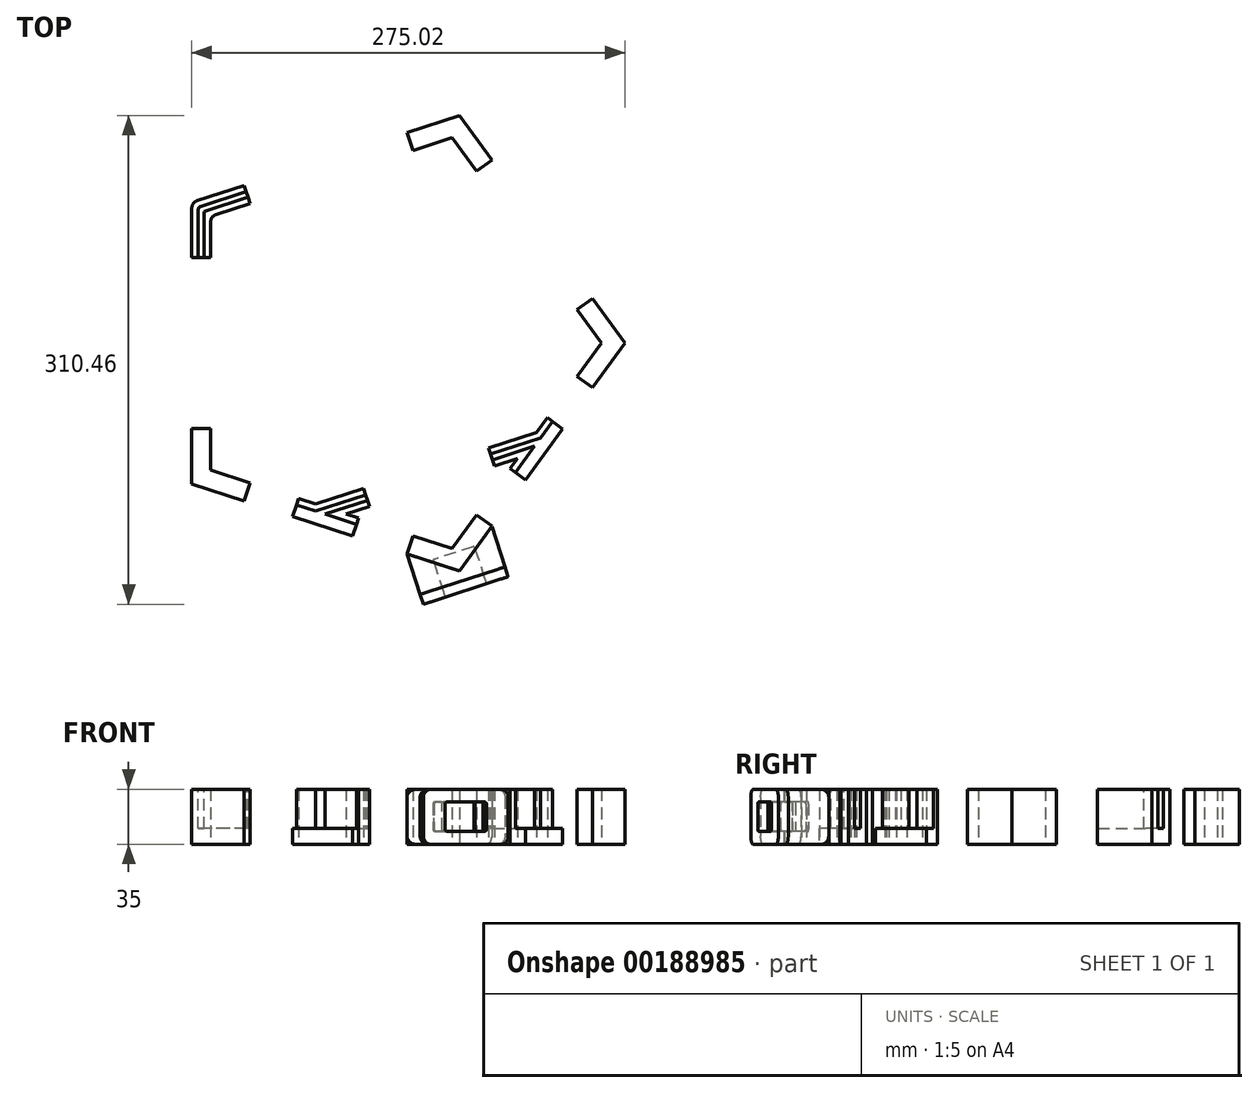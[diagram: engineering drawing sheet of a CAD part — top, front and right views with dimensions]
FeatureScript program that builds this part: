
annotation { "Feature Type Name" : "Feature", "Feature Type Description" : "" }
export const myFeature = defineFeature(function(context is Context, id is Id, definition is map)
    precondition{}
    {
        {
            var Q0;
            Q0=qCreatedBy(makeId("Top.planeOp"),FACE);
            var sketch = newSketch(context, id + "F0", { "sketchPlane" : qUnion([Q0])});
            skCircle(sketch, "E0.cCircle", {"center": v(0, 0) * mm, "radius": 117 * mm, "construction": true});
            skLineSegment(sketch, "E0.0", {"start": v(-117, 85) * mm, "end": v(44.69, 137.53) * mm, "construction": true});
            skLineSegment(sketch, "E0.1", {"start": v(44.69, 137.53) * mm, "end": v(144.61, 0) * mm, "construction": true});
            skLineSegment(sketch, "E0.2", {"start": v(144.61, 0) * mm, "end": v(44.69, -137.53) * mm, "construction": true});
            skLineSegment(sketch, "E0.3", {"start": v(44.69, -137.53) * mm, "end": v(-117, -85) * mm, "construction": true});
            skLineSegment(sketch, "E0.4", {"start": v(-117, -85) * mm, "end": v(-117, 85) * mm, "construction": true});
            skPoint(sketch, "E0.0.midPoint", {"position": v(-36.15, 111.27) * mm});
            skLineSegment(sketch, "E1", {"start": v(-123, 89.36) * mm, "end": v(-89.7, 100.17) * mm});
            skLineSegment(sketch, "E2", {"start": v(-123, 54.36) * mm, "end": v(-123, 89.36) * mm});
            skLineSegment(sketch, "E3.MirrorCS", {"start": v(-111, 54.36) * mm, "end": v(-111, 80.64) * mm});
            skLineSegment(sketch, "E4.MirrorCS", {"start": v(-111, 80.64) * mm, "end": v(-86, 88.76) * mm});
            skPoint(sketch, "E5.orphan", {"position": v(-127.63, 87.85) * mm});
            skPoint(sketch, "E6.orphan", {"position": v(-123, 104.04) * mm});
            skPoint(sketch, "E7.orphan", {"position": v(-111, 104.04) * mm});
            skPoint(sketch, "E8.orphan", {"position": v(-123.92, 76.44) * mm});
            skLineSegment(sketch, "E9", {"start": v(-123, 54.36) * mm, "end": v(-111, 54.36) * mm});
            skLineSegment(sketch, "E10", {"start": v(-86, 88.76) * mm, "end": v(-89.7, 100.17) * mm});
            skPoint(sketch, "E11.MirrorP", {"position": v(-127.63, -87.85) * mm});
            skPoint(sketch, "E12.MirrorP", {"position": v(-123, -104.04) * mm});
            skPoint(sketch, "E13.MirrorP", {"position": v(-111, -104.04) * mm});
            skPoint(sketch, "E14.MirrorP", {"position": v(-123.92, -76.44) * mm});
            skLineSegment(sketch, "E15.MirrorCS", {"start": v(-86, -88.76) * mm, "end": v(-89.7, -100.17) * mm});
            skLineSegment(sketch, "E16.MirrorCS", {"start": v(-123, -54.36) * mm, "end": v(-111, -54.36) * mm});
            skLineSegment(sketch, "E17.MirrorCS", {"start": v(-111, -80.64) * mm, "end": v(-86, -88.76) * mm});
            skLineSegment(sketch, "E18.MirrorCS", {"start": v(-111, -54.36) * mm, "end": v(-111, -80.64) * mm});
            skLineSegment(sketch, "E19.MirrorCS", {"start": v(-123, -54.36) * mm, "end": v(-123, -89.36) * mm});
            skLineSegment(sketch, "E20.MirrorCS", {"start": v(-123, -89.36) * mm, "end": v(-89.7, -100.17) * mm});
            skLineSegment(sketch, "E21.MirrorCS", {"start": v(-117, 85) * mm, "end": v(-117, -85) * mm, "construction": true});
            skLineSegment(sketch, "E22.MirrorCS", {"start": v(-117, -85) * mm, "end": v(44.69, -137.53) * mm, "construction": true});
            skLineSegment(sketch, "E23", {"start": v(-36.15, -111.27) * mm, "end": v(-46.52, -143.17) * mm, "construction": true});
            skLineSegment(sketch, "E24.MirrorCS", {"start": v(44.69, -137.53) * mm, "end": v(144.61, 0) * mm, "construction": true});
            skPoint(sketch, "E25.MirrorP", {"position": v(51.62, -146.1) * mm});
            skLineSegment(sketch, "E26.MirrorCS", {"start": v(67.55, -116.27) * mm, "end": v(46.98, -144.59) * mm});
            skPoint(sketch, "E27.MirrorP", {"position": v(160.66, 11.88) * mm});
            skLineSegment(sketch, "E28.MirrorCS", {"start": v(17.4, -122.36) * mm, "end": v(13.7, -133.77) * mm});
            skLineSegment(sketch, "E29.MirrorCS", {"start": v(121.75, 21.26) * mm, "end": v(131.45, 28.32) * mm});
            skLineSegment(sketch, "E30.MirrorCS", {"start": v(131.45, -28.32) * mm, "end": v(121.75, -21.26) * mm});
            skLineSegment(sketch, "E31.MirrorCS", {"start": v(137.2, 0) * mm, "end": v(121.75, 21.26) * mm});
            skLineSegment(sketch, "E32.MirrorCS", {"start": v(121.75, -21.26) * mm, "end": v(137.2, 0) * mm});
            skLineSegment(sketch, "E33.MirrorCS", {"start": v(131.45, -28.32) * mm, "end": v(152.03, 0) * mm});
            skLineSegment(sketch, "E34.MirrorCS", {"start": v(152.03, 0) * mm, "end": v(131.45, 28.32) * mm});
            skPoint(sketch, "E35.MirrorP", {"position": v(28.64, -149.41) * mm});
            skPoint(sketch, "E36.MirrorP", {"position": v(55.33, -134.68) * mm});
            skPoint(sketch, "E37.MirrorP", {"position": v(150.95, 18.93) * mm});
            skPoint(sketch, "E38.MirrorP", {"position": v(154.9, -3.95) * mm});
            skLineSegment(sketch, "E39.MirrorCS", {"start": v(67.55, -116.27) * mm, "end": v(57.84, -109.22) * mm});
            skLineSegment(sketch, "E40.MirrorCS", {"start": v(46.98, -144.59) * mm, "end": v(13.7, -133.77) * mm});
            skLineSegment(sketch, "E41.MirrorCS", {"start": v(42.4, -130.48) * mm, "end": v(17.4, -122.36) * mm});
            skLineSegment(sketch, "E42.MirrorCS", {"start": v(57.84, -109.22) * mm, "end": v(42.4, -130.48) * mm});
            skPoint(sketch, "E43.MirrorP", {"position": v(38.35, -156.47) * mm});
            skPoint(sketch, "E44.MirrorP", {"position": v(145.19, -11) * mm});
            skLineSegment(sketch, "E45", {"start": v(94.65, 68.77) * mm, "end": v(113.34, 82.34) * mm, "construction": true});
            skLineSegment(sketch, "E46.MirrorCS", {"start": v(44.69, 137.53) * mm, "end": v(-117, 85) * mm, "construction": true});
            skLineSegment(sketch, "E47.MirrorCS", {"start": v(46.98, 144.59) * mm, "end": v(67.55, 116.27) * mm});
            skPoint(sketch, "E48.MirrorP", {"position": v(60.94, 149.12) * mm});
            skPoint(sketch, "E49.MirrorP", {"position": v(44.11, 148.53) * mm});
            skPoint(sketch, "E50.MirrorP", {"position": v(34.4, 141.48) * mm});
            skLineSegment(sketch, "E51.MirrorCS", {"start": v(13.7, 133.77) * mm, "end": v(46.98, 144.59) * mm});
            skLineSegment(sketch, "E52.MirrorCS", {"start": v(42.4, 130.48) * mm, "end": v(57.84, 109.22) * mm});
            skPoint(sketch, "E53.MirrorP", {"position": v(64.65, 137.71) * mm});
            skLineSegment(sketch, "E54.MirrorCS", {"start": v(144.61, 0) * mm, "end": v(44.69, 137.53) * mm, "construction": true});
            skLineSegment(sketch, "E55.MirrorCS", {"start": v(57.84, 109.22) * mm, "end": v(67.55, 116.27) * mm});
            skLineSegment(sketch, "E56.MirrorCS", {"start": v(17.4, 122.36) * mm, "end": v(42.4, 130.48) * mm});
            skLineSegment(sketch, "E57.MirrorCS", {"start": v(13.7, 133.77) * mm, "end": v(17.4, 122.36) * mm});
            skLineSegment(sketch, "E58", {"start": v(-81.04, -120.55) * mm, "end": v(144.28, -47.34) * mm, "construction": true});
            skLineSegment(sketch, "E59", {"start": v(44.69, -137.53) * mm, "end": v(54.4, -134.38) * mm});
            skLineSegment(sketch, "E60", {"start": v(-20.95, -122.51) * mm, "end": v(-59, -110.15) * mm});
            skLineSegment(sketch, "E61.MirrorCS", {"start": v(-17.24, -111.1) * mm, "end": v(-24.89, -108.62) * mm});
            skLineSegment(sketch, "E62", {"start": v(-44.3, -102.3) * mm, "end": v(-13.87, -92.42) * mm});
            skLineSegment(sketch, "E63.MirrorCS", {"start": v(-34.6, -111.77) * mm, "end": v(-34.58, -111.77) * mm});
            skLineSegment(sketch, "E64", {"start": v(-55.29, -98.74) * mm, "end": v(-59, -110.15) * mm});
            skLineSegment(sketch, "E65", {"start": v(-17.24, -111.1) * mm, "end": v(-20.95, -122.51) * mm});
            skPoint(sketch, "E66.orphan", {"position": v(-40.6, -113.72) * mm});
            skLineSegment(sketch, "E67.trimOffspring", {"start": v(-24.89, -108.62) * mm, "end": v(-10.16, -103.83) * mm});
            skLineSegment(sketch, "E68.trimOffspring", {"start": v(-44.3, -102.3) * mm, "end": v(-55.29, -98.74) * mm});
            skLineSegment(sketch, "E69", {"start": v(-13.87, -92.42) * mm, "end": v(-10.16, -103.83) * mm});
            skLineSegment(sketch, "E70", {"start": v(-36.15, 111.27) * mm, "end": v(42.4, -130.48) * mm, "construction": true});
            skLineSegment(sketch, "E71.MirrorCS", {"start": v(93.69, -70.1) * mm, "end": v(93.67, -70.1) * mm});
            skLineSegment(sketch, "E72.MirrorCS", {"start": v(102.77, -47.39) * mm, "end": v(112.47, -54.44) * mm});
            skLineSegment(sketch, "E73.MirrorCS", {"start": v(95.98, -56.73) * mm, "end": v(102.77, -47.39) * mm});
            skLineSegment(sketch, "E74.MirrorCS", {"start": v(79.25, -79.75) * mm, "end": v(88.96, -86.8) * mm});
            skLineSegment(sketch, "E75.MirrorCS", {"start": v(95.98, -56.73) * mm, "end": v(65.55, -66.62) * mm});
            skPoint(sketch, "E76.MirrorP", {"position": v(99.69, -68.14) * mm});
            skLineSegment(sketch, "E77.MirrorCS", {"start": v(83.98, -73.24) * mm, "end": v(69.25, -78.03) * mm});
            skLineSegment(sketch, "E78.MirrorCS", {"start": v(88.96, -86.8) * mm, "end": v(112.47, -54.44) * mm});
            skLineSegment(sketch, "E79.MirrorCS", {"start": v(65.55, -66.62) * mm, "end": v(69.25, -78.03) * mm});
            skLineSegment(sketch, "E80.MirrorCS", {"start": v(79.25, -79.75) * mm, "end": v(83.98, -73.24) * mm});
            skLineSegment(sketch, "E81", {"start": v(22.07, -159.6) * mm, "end": v(75.94, -142.1) * mm});
            skLineSegment(sketch, "E82", {"start": v(67.59, -116.39) * mm, "end": v(75.94, -142.1) * mm});
            skLineSegment(sketch, "E83.MirrorCS", {"start": v(13.73, -133.89) * mm, "end": v(22.08, -159.6) * mm});
            skLineSegment(sketch, "E84", {"start": v(13.73, -133.89) * mm, "end": v(47.02, -144.7) * mm});
            skLineSegment(sketch, "E85", {"start": v(67.59, -116.39) * mm, "end": v(47.02, -144.7) * mm});
            skPoint(sketch, "E86.orphan", {"position": v(67.68, -116.27) * mm});
            skPoint(sketch, "E87.orphan", {"position": v(13.7, -133.77) * mm});
            skSolve(sketch);
        }
        {
            var Q0;
            Q0=qSketchRegion(id+"F0",true);
            extrude(context, id + "F1", {"entities" : qUnion([Q0]), "depth" : 35 * mm});
        }
        {
            var Q0;
            Q0=makeQuery(id+"F1.opExtrude","CAP_FACE",FACE,{"disambiguationData":[OSD([sQuery(id+"F0.wireOp",EDGE,"E1"),sQuery(id+"F0.wireOp",EDGE,"E2"),sQuery(id+"F0.wireOp",EDGE,"E3.MirrorCS"),sQuery(id+"F0.wireOp",EDGE,"E4.MirrorCS"),sQuery(id+"F0.wireOp",EDGE,"E9"),sQuery(id+"F0.wireOp",EDGE,"E10")])],"isStart":false});
            var sketch = newSketch(context, id + "F2", { "sketchPlane" : qUnion([Q0])});
            skLineSegment(sketch, "E88", {"start": v(-117, 54.36) * mm, "end": v(-117, 85) * mm});
            skLineSegment(sketch, "E89", {"start": v(-87.85, 94.47) * mm, "end": v(-117, 85) * mm});
            skPoint(sketch, "E90.orphan", {"position": v(-117, 84.36) * mm});
            skPoint(sketch, "E91.orphan", {"position": v(-118.96, 84.36) * mm});
            skArc(sketch, "E92.0.startCap", {"start": v(-115.12, 54.36) * mm, "mid": v(-117, 52.48) * mm, "end": v(-118.87, 54.36) * mm});
            skArc(sketch, "E92.0.endCap", {"start": v(-118.87, 85) * mm, "mid": v(-117, 86.87) * mm, "end": v(-115.12, 85) * mm});
            skLineSegment(sketch, "E92.0.left", {"start": v(-118.87, 54.36) * mm, "end": v(-118.87, 85) * mm});
            skLineSegment(sketch, "E92.0.right", {"start": v(-115.12, 54.36) * mm, "end": v(-115.12, 85) * mm});
            skArc(sketch, "E92.1.startCap", {"start": v(-88.43, 96.25) * mm, "mid": v(-86.07, 95.05) * mm, "end": v(-87.27, 92.69) * mm});
            skArc(sketch, "E92.1.endCap", {"start": v(-116.41, 83.22) * mm, "mid": v(-118.78, 84.42) * mm, "end": v(-117.57, 86.78) * mm});
            skLineSegment(sketch, "E92.1.left", {"start": v(-87.27, 92.69) * mm, "end": v(-116.41, 83.22) * mm});
            skLineSegment(sketch, "E92.1.right", {"start": v(-88.43, 96.25) * mm, "end": v(-117.57, 86.78) * mm});
            skLineSegment(sketch, "E93", {"start": v(-44.3, -108.62) * mm, "end": v(99.69, -61.83) * mm});
            skLineSegment(sketch, "E94", {"start": v(113.08, -43.4) * mm, "end": v(77.1, -92.92) * mm});
            skLineSegment(sketch, "E95", {"start": v(-66.96, -101.26) * mm, "end": v(-1.1, -122.66) * mm});
            skPoint(sketch, "E96.end.orphan", {"position": v(64.77, -144.06) * mm});
            skArc(sketch, "E97.0.startCap", {"start": v(-43.73, -110.4) * mm, "mid": v(-46.09, -109.2) * mm, "end": v(-44.88, -106.83) * mm});
            skArc(sketch, "E97.0.endCap", {"start": v(99.1, -60.05) * mm, "mid": v(101.47, -61.25) * mm, "end": v(100.27, -63.62) * mm});
            skLineSegment(sketch, "E97.0.left", {"start": v(-44.88, -106.83) * mm, "end": v(99.1, -60.05) * mm});
            skLineSegment(sketch, "E97.0.right", {"start": v(-43.73, -110.4) * mm, "end": v(100.27, -63.62) * mm});
            skArc(sketch, "E97.1.startCap", {"start": v(-67.54, -103.04) * mm, "mid": v(-68.74, -100.68) * mm, "end": v(-66.38, -99.47) * mm});
            skArc(sketch, "E97.1.endCap", {"start": v(-0.51, -120.87) * mm, "mid": v(0.7, -123.24) * mm, "end": v(-1.67, -124.44) * mm});
            skLineSegment(sketch, "E97.1.left", {"start": v(-66.38, -99.47) * mm, "end": v(-0.51, -120.87) * mm});
            skLineSegment(sketch, "E97.1.right", {"start": v(-67.54, -103.04) * mm, "end": v(-1.67, -124.44) * mm});
            skArc(sketch, "E97.2.startCap", {"start": v(111.56, -42.3) * mm, "mid": v(114.18, -41.88) * mm, "end": v(114.6, -44.5) * mm});
            skArc(sketch, "E97.2.endCap", {"start": v(78.61, -94.03) * mm, "mid": v(76, -94.44) * mm, "end": v(75.58, -91.82) * mm});
            skLineSegment(sketch, "E97.2.left", {"start": v(114.6, -44.5) * mm, "end": v(78.61, -94.03) * mm});
            skLineSegment(sketch, "E97.2.right", {"start": v(111.56, -42.3) * mm, "end": v(75.58, -91.82) * mm});
            skSolve(sketch);
        }
        {
            var Q0;
            {var subQ0=sQuery(id+"F2.wireOp",EDGE,"E97.1.endCap");Q0=makeQuery(id+"F2.imprint","IMPRINT",FACE,{"disambiguationData":[TD([[makeQuery(id+"F2.imprint","IMPRINT",EDGE,{"derivedFrom":subQ0}),-1.0]])]});}
            var Q1;
            {var subQ5=sQuery(id+"F2.wireOp",EDGE,"E97.1.startCap");Q1=makeQuery(id+"F2.imprint","IMPRINT",FACE,{"disambiguationData":[TD([[makeQuery(id+"F2.imprint","IMPRINT",EDGE,{"derivedFrom":subQ5}),-1.0]])]});}
            var Q2;
            {var subQ8=sQuery(id+"F2.wireOp",EDGE,"E97.2.startCap");Q2=makeQuery(id+"F2.imprint","IMPRINT",FACE,{"disambiguationData":[TD([[makeQuery(id+"F2.imprint","IMPRINT",EDGE,{"derivedFrom":subQ8}),-1.0]])]});}
            var Q3;
            {var subQ5=sQuery(id+"F2.wireOp",EDGE,"E97.2.endCap");Q3=makeQuery(id+"F2.imprint","IMPRINT",FACE,{"disambiguationData":[TD([[makeQuery(id+"F2.imprint","IMPRINT",EDGE,{"derivedFrom":subQ5}),-1.0]])]});}
            var Q4;
            {var subQ3=sQuery(id+"F2.wireOp",EDGE,"E89");var subQ7=sQuery(id+"F2.wireOp",EDGE,"E88");var subQ8=makeQuery(id+"F2.imprint","INTERSECT",VERTEX,{"derivedFrom":[subQ7,subQ3]});Q4=makeQuery(id+"F2.imprint","IMPRINT",FACE,{"disambiguationData":[TD([[makeQuery(id+"F2.imprint","IMPRINT",EDGE,{"disambiguationData":[TD([[subQ8,1.0]])],"derivedFrom":subQ7}),-1.0]])]});}
            var Q5;
            {var subQ0=sQuery(id+"F2.wireOp",EDGE,"E97.1.left");var subQ1=sQuery(id+"F2.wireOp",EDGE,"E93");var subQ2=makeQuery(id+"F2.imprint","INTERSECT",VERTEX,{"derivedFrom":[subQ1,subQ0]});Q5=makeQuery(id+"F2.imprint","IMPRINT",FACE,{"disambiguationData":[TD([[makeQuery(id+"F2.imprint","IMPRINT",EDGE,{"disambiguationData":[TD([[subQ2,-1.0]])],"derivedFrom":subQ1}),1.0]])]});}
            var Q6;
            {var subQ2=sQuery(id+"F2.wireOp",EDGE,"E88");var subQ6=sQuery(id+"F2.wireOp",EDGE,"E89");var subQ8=makeQuery(id+"F2.imprint","INTERSECT",VERTEX,{"derivedFrom":[subQ2,subQ6]});Q6=makeQuery(id+"F2.imprint","IMPRINT",FACE,{"disambiguationData":[TD([[makeQuery(id+"F2.imprint","IMPRINT",EDGE,{"disambiguationData":[TD([[subQ8,1.0]])],"derivedFrom":subQ2}),1.0]])]});}
            var Q7;
            {var subQ3=sQuery(id+"F2.wireOp",EDGE,"E95");var subQ7=sQuery(id+"F2.wireOp",EDGE,"E93");var subQ8=makeQuery(id+"F2.imprint","INTERSECT",VERTEX,{"derivedFrom":[subQ7,subQ3]});Q7=makeQuery(id+"F2.imprint","IMPRINT",FACE,{"disambiguationData":[TD([[makeQuery(id+"F2.imprint","IMPRINT",EDGE,{"disambiguationData":[TD([[subQ8,-1.0]])],"derivedFrom":subQ7}),1.0]])]});}
            var Q8;
            {var subQ0=sQuery(id+"F2.wireOp",EDGE,"E95");var subQ1=sQuery(id+"F2.wireOp",EDGE,"E93");var subQ2=makeQuery(id+"F2.imprint","INTERSECT",VERTEX,{"derivedFrom":[subQ1,subQ0]});Q8=makeQuery(id+"F2.imprint","IMPRINT",FACE,{"disambiguationData":[TD([[makeQuery(id+"F2.imprint","IMPRINT",EDGE,{"disambiguationData":[TD([[subQ2,-1.0]])],"derivedFrom":subQ1}),-1.0]])]});}
            var Q9;
            {var subQ5=sQuery(id+"F2.wireOp",EDGE,"E94");var subQ6=sQuery(id+"F2.wireOp",EDGE,"E93");var subQ7=makeQuery(id+"F2.imprint","INTERSECT",VERTEX,{"derivedFrom":[subQ6,subQ5]});Q9=makeQuery(id+"F2.imprint","IMPRINT",FACE,{"disambiguationData":[TD([[makeQuery(id+"F2.imprint","IMPRINT",EDGE,{"disambiguationData":[TD([[subQ7,1.0]])],"derivedFrom":subQ6}),1.0]])]});}
            var Q10;
            {var subQ0=sQuery(id+"F2.wireOp",EDGE,"E94");var subQ1=sQuery(id+"F2.wireOp",EDGE,"E93");var subQ2=makeQuery(id+"F2.imprint","INTERSECT",VERTEX,{"derivedFrom":[subQ1,subQ0]});Q10=makeQuery(id+"F2.imprint","IMPRINT",FACE,{"disambiguationData":[TD([[makeQuery(id+"F2.imprint","IMPRINT",EDGE,{"disambiguationData":[TD([[subQ2,1.0]])],"derivedFrom":subQ1}),-1.0]])]});}
            var Q11;
            {var subQ4=sQuery(id+"F2.wireOp",EDGE,"E94");var subQ5=makeQuery(id+"F2.imprint","INTERSECT",VERTEX,{"derivedFrom":[sQuery(id+"F2.wireOp",EDGE,"E93"),subQ4]});Q11=makeQuery(id+"F2.imprint","IMPRINT",FACE,{"disambiguationData":[TD([[makeQuery(id+"F2.imprint","IMPRINT",EDGE,{"disambiguationData":[TD([[subQ5,1.0]])],"derivedFrom":subQ4}),1.0]])]});}
            var Q12;
            {var subQ1=sQuery(id+"F2.wireOp",EDGE,"E95");var subQ4=makeQuery(id+"F2.imprint","INTERSECT",VERTEX,{"derivedFrom":[sQuery(id+"F2.wireOp",EDGE,"E93"),subQ1]});Q12=makeQuery(id+"F2.imprint","IMPRINT",FACE,{"disambiguationData":[TD([[makeQuery(id+"F2.imprint","IMPRINT",EDGE,{"disambiguationData":[TD([[subQ4,1.0]])],"derivedFrom":subQ1}),-1.0]])]});}
            var Q13;
            {var subQ5=sQuery(id+"F2.wireOp",EDGE,"E92.0.left");Q13=makeQuery(id+"F2.imprint","IMPRINT",FACE,{"disambiguationData":[TD([[makeQuery(id+"F2.imprint","IMPRINT",EDGE,{"derivedFrom":subQ5}),-1.0]])]});}
            var Q14;
            {var subQ5=sQuery(id+"F2.wireOp",EDGE,"E88");var subQ7=makeQuery(id+"F1.opExtrude","CAP_EDGE",EDGE,{"disambiguationData":[OSD([sQuery(id+"F0.wireOp",EDGE,"E9")])],"isStart":false});var subQ9=makeQuery(id+"F2.imprint","INTERSECT",VERTEX,{"derivedFrom":[subQ7,subQ5]});Q14=makeQuery(id+"F2.imprint","IMPRINT",FACE,{"disambiguationData":[TD([[makeQuery(id+"F2.imprint","IMPRINT",EDGE,{"disambiguationData":[TD([[subQ9,-1.0]])],"derivedFrom":subQ5}),-1.0]])]});}
            var Q15;
            {var subQ5=sQuery(id+"F2.wireOp",EDGE,"E92.1.right");Q15=makeQuery(id+"F2.imprint","IMPRINT",FACE,{"disambiguationData":[TD([[makeQuery(id+"F2.imprint","IMPRINT",EDGE,{"derivedFrom":subQ5}),1.0]])]});}
            var Q16;
            {var subQ1=makeQuery(id+"F1.opExtrude","CAP_EDGE",EDGE,{"disambiguationData":[OSD([sQuery(id+"F0.wireOp",EDGE,"E10")])],"isStart":false});var subQ7=sQuery(id+"F2.wireOp",EDGE,"E89");var subQ9=makeQuery(id+"F2.imprint","INTERSECT",VERTEX,{"derivedFrom":[subQ1,subQ7]});Q16=makeQuery(id+"F2.imprint","IMPRINT",FACE,{"disambiguationData":[TD([[makeQuery(id+"F2.imprint","IMPRINT",EDGE,{"disambiguationData":[TD([[subQ9,-1.0]])],"derivedFrom":subQ7}),1.0]])]});}
            var Q17;
            {var subQ0=sQuery(id+"F2.wireOp",EDGE,"E92.0.startCap");Q17=makeQuery(id+"F2.imprint","IMPRINT",FACE,{"disambiguationData":[TD([[makeQuery(id+"F2.imprint","IMPRINT",EDGE,{"derivedFrom":subQ0}),-1.0]])]});}
            var Q18;
            {var subQ0=sQuery(id+"F2.wireOp",EDGE,"E92.1.startCap");Q18=makeQuery(id+"F2.imprint","IMPRINT",FACE,{"disambiguationData":[TD([[makeQuery(id+"F2.imprint","IMPRINT",EDGE,{"derivedFrom":subQ0}),-1.0]])]});}
            extrude(context, id + "F3", {"entities" : qUnion([Q0, Q1, Q2, Q3, Q4, Q5, Q6, Q7, Q8, Q9, Q10, Q11, Q12, Q13, Q14, Q15, Q16, Q17, Q18]), "operationType" : NewBodyOperationType.REMOVE, "oppositeDirection" : true, "depth" : 25 * mm});
        }
        {
            var Q0;
            Q0=makeQuery(id+"F1.opExtrude","SWEPT_EDGE",EDGE,{"disambiguationData":[OSD([sQuery(id+"F0.wireOp",EDGE,"E3.MirrorCS"),sQuery(id+"F0.wireOp",EDGE,"E4.MirrorCS")])]});
            var Q1;
            Q1=makeQuery(id+"F1.opExtrude","SWEPT_EDGE",EDGE,{"disambiguationData":[OSD([sQuery(id+"F0.wireOp",EDGE,"E1"),sQuery(id+"F0.wireOp",EDGE,"E2")])]});
            fillet(context, id + "F4", {"entities" : qUnion([Q0, Q1]), "radius" : 5 * mm, "tangentPropagation" : true, "allowEdgeOverflow" : false});
        }
        {
            var Q0;
            Q0=makeQuery(id+"F1.opExtrude","CAP_FACE",FACE,{"disambiguationData":[OSD([sQuery(id+"F0.wireOp",EDGE,"E60"),sQuery(id+"F0.wireOp",EDGE,"E61.MirrorCS"),sQuery(id+"F0.wireOp",EDGE,"E62"),sQuery(id+"F0.wireOp",EDGE,"E64"),sQuery(id+"F0.wireOp",EDGE,"E65"),sQuery(id+"F0.wireOp",EDGE,"E67.trimOffspring"),sQuery(id+"F0.wireOp",EDGE,"E68.trimOffspring"),sQuery(id+"F0.wireOp",EDGE,"E69")])],"isStart":false});
            var sketch = newSketch(context, id + "F5", { "sketchPlane" : qUnion([Q0])});
            skLineSegment(sketch, "E98", {"start": v(-44.3, -108.62) * mm, "end": v(99.69, -61.83) * mm});
            skLineSegment(sketch, "E99", {"start": v(112.9, -43.64) * mm, "end": v(76.92, -93.16) * mm});
            skLineSegment(sketch, "E100", {"start": v(-67.46, -101.1) * mm, "end": v(-1.6, -122.5) * mm});
            skPoint(sketch, "E101.end.orphan", {"position": v(64.27, -143.9) * mm});
            skArc(sketch, "E102.0.startCap", {"start": v(-43.73, -110.4) * mm, "mid": v(-46.09, -109.2) * mm, "end": v(-44.88, -106.83) * mm});
            skArc(sketch, "E102.0.endCap", {"start": v(99.1, -60.05) * mm, "mid": v(101.47, -61.25) * mm, "end": v(100.27, -63.62) * mm});
            skLineSegment(sketch, "E102.0.left", {"start": v(-44.88, -106.83) * mm, "end": v(99.1, -60.05) * mm});
            skLineSegment(sketch, "E102.0.right", {"start": v(-43.73, -110.4) * mm, "end": v(100.27, -63.62) * mm});
            skArc(sketch, "E102.1.startCap", {"start": v(-68.04, -102.88) * mm, "mid": v(-69.25, -100.51) * mm, "end": v(-66.88, -99.3) * mm});
            skArc(sketch, "E102.1.endCap", {"start": v(-1.02, -120.71) * mm, "mid": v(0.19, -123.07) * mm, "end": v(-2.18, -124.28) * mm});
            skLineSegment(sketch, "E102.1.left", {"start": v(-66.88, -99.3) * mm, "end": v(-1.02, -120.71) * mm});
            skLineSegment(sketch, "E102.1.right", {"start": v(-68.04, -102.88) * mm, "end": v(-2.18, -124.28) * mm});
            skArc(sketch, "E102.2.startCap", {"start": v(111.4, -42.53) * mm, "mid": v(114, -42.12) * mm, "end": v(114.42, -44.74) * mm});
            skArc(sketch, "E102.2.endCap", {"start": v(78.44, -94.27) * mm, "mid": v(75.82, -94.68) * mm, "end": v(75.4, -92.06) * mm});
            skLineSegment(sketch, "E102.2.left", {"start": v(114.42, -44.74) * mm, "end": v(78.44, -94.27) * mm});
            skLineSegment(sketch, "E102.2.right", {"start": v(111.4, -42.53) * mm, "end": v(75.4, -92.06) * mm});
            skSolve(sketch);
        }
        {
            var Q0;
            {var subQ1=sQuery(id+"F5.wireOp",EDGE,"E102.1.startCap");Q0=makeQuery(id+"F5.imprint","IMPRINT",FACE,{"disambiguationData":[TD([[makeQuery(id+"F5.imprint","IMPRINT",EDGE,{"derivedFrom":subQ1}),-1.0]])]});}
            var Q1;
            {var subQ5=sQuery(id+"F5.wireOp",EDGE,"E102.0.startCap");var subQ7=sQuery(id+"F5.wireOp",EDGE,"E100");var subQ8=makeQuery(id+"F5.imprint","INTERSECT",VERTEX,{"derivedFrom":[subQ7,subQ5]});Q1=makeQuery(id+"F5.imprint","IMPRINT",FACE,{"disambiguationData":[TD([[makeQuery(id+"F5.imprint","IMPRINT",EDGE,{"disambiguationData":[TD([[subQ8,1.0]])],"derivedFrom":subQ7}),1.0]])]});}
            var Q2;
            {var subQ0=sQuery(id+"F5.wireOp",EDGE,"E102.0.startCap");var subQ1=sQuery(id+"F5.wireOp",EDGE,"E100");var subQ2=makeQuery(id+"F5.imprint","INTERSECT",VERTEX,{"derivedFrom":[subQ1,subQ0]});Q2=makeQuery(id+"F5.imprint","IMPRINT",FACE,{"disambiguationData":[TD([[makeQuery(id+"F5.imprint","IMPRINT",EDGE,{"disambiguationData":[TD([[subQ2,1.0]])],"derivedFrom":subQ1}),-1.0]])]});}
            var Q3;
            {var subQ1=sQuery(id+"F5.wireOp",EDGE,"E100");var subQ6=makeQuery(id+"F5.imprint","INTERSECT",VERTEX,{"derivedFrom":[sQuery(id+"F5.wireOp",EDGE,"E98"),subQ1]});Q3=makeQuery(id+"F5.imprint","IMPRINT",FACE,{"disambiguationData":[TD([[makeQuery(id+"F5.imprint","IMPRINT",EDGE,{"disambiguationData":[TD([[subQ6,1.0]])],"derivedFrom":subQ1}),-1.0]])]});}
            var Q4;
            {var subQ3=sQuery(id+"F5.wireOp",EDGE,"E100");var subQ5=sQuery(id+"F5.wireOp",EDGE,"E98");var subQ6=makeQuery(id+"F5.imprint","INTERSECT",VERTEX,{"derivedFrom":[subQ5,subQ3]});Q4=makeQuery(id+"F5.imprint","IMPRINT",FACE,{"disambiguationData":[TD([[makeQuery(id+"F5.imprint","IMPRINT",EDGE,{"disambiguationData":[TD([[subQ6,-1.0]])],"derivedFrom":subQ5}),1.0]])]});}
            var Q5;
            {var subQ0=sQuery(id+"F5.wireOp",EDGE,"E100");var subQ1=sQuery(id+"F5.wireOp",EDGE,"E98");var subQ2=makeQuery(id+"F5.imprint","INTERSECT",VERTEX,{"derivedFrom":[subQ1,subQ0]});Q5=makeQuery(id+"F5.imprint","IMPRINT",FACE,{"disambiguationData":[TD([[makeQuery(id+"F5.imprint","IMPRINT",EDGE,{"disambiguationData":[TD([[subQ2,-1.0]])],"derivedFrom":subQ1}),-1.0]])]});}
            var Q6;
            {var subQ0=sQuery(id+"F5.wireOp",EDGE,"E102.1.left");var subQ1=sQuery(id+"F5.wireOp",EDGE,"E98");var subQ2=makeQuery(id+"F5.imprint","INTERSECT",VERTEX,{"derivedFrom":[subQ1,subQ0]});Q6=makeQuery(id+"F5.imprint","IMPRINT",FACE,{"disambiguationData":[TD([[makeQuery(id+"F5.imprint","IMPRINT",EDGE,{"disambiguationData":[TD([[subQ2,-1.0]])],"derivedFrom":subQ1}),1.0]])]});}
            var Q7;
            {var subQ0=sQuery(id+"F5.wireOp",EDGE,"E102.1.left");var subQ1=sQuery(id+"F5.wireOp",EDGE,"E98");var subQ2=makeQuery(id+"F5.imprint","INTERSECT",VERTEX,{"derivedFrom":[subQ1,subQ0]});Q7=makeQuery(id+"F5.imprint","IMPRINT",FACE,{"disambiguationData":[TD([[makeQuery(id+"F5.imprint","IMPRINT",EDGE,{"disambiguationData":[TD([[subQ2,-1.0]])],"derivedFrom":subQ1}),-1.0]])]});}
            var Q8;
            {var subQ0=sQuery(id+"F5.wireOp",EDGE,"E102.0.right");var subQ1=sQuery(id+"F5.wireOp",EDGE,"E100");var subQ2=makeQuery(id+"F5.imprint","INTERSECT",VERTEX,{"derivedFrom":[subQ1,subQ0]});Q8=makeQuery(id+"F5.imprint","IMPRINT",FACE,{"disambiguationData":[TD([[makeQuery(id+"F5.imprint","IMPRINT",EDGE,{"disambiguationData":[TD([[subQ2,-1.0]])],"derivedFrom":subQ1}),1.0]])]});}
            var Q9;
            {var subQ5=sQuery(id+"F5.wireOp",EDGE,"E102.0.right");var subQ7=sQuery(id+"F5.wireOp",EDGE,"E100");var subQ8=makeQuery(id+"F5.imprint","INTERSECT",VERTEX,{"derivedFrom":[subQ7,subQ5]});Q9=makeQuery(id+"F5.imprint","IMPRINT",FACE,{"disambiguationData":[TD([[makeQuery(id+"F5.imprint","IMPRINT",EDGE,{"disambiguationData":[TD([[subQ8,-1.0]])],"derivedFrom":subQ7}),-1.0]])]});}
            var Q10;
            {var subQ1=sQuery(id+"F5.wireOp",EDGE,"E102.1.endCap");Q10=makeQuery(id+"F5.imprint","IMPRINT",FACE,{"disambiguationData":[TD([[makeQuery(id+"F5.imprint","IMPRINT",EDGE,{"derivedFrom":subQ1}),-1.0]])]});}
            var Q11;
            {var subQ0=sQuery(id+"F5.wireOp",EDGE,"E102.2.right");var subQ1=sQuery(id+"F5.wireOp",EDGE,"E98");var subQ2=makeQuery(id+"F5.imprint","INTERSECT",VERTEX,{"derivedFrom":[subQ1,subQ0]});Q11=makeQuery(id+"F5.imprint","IMPRINT",FACE,{"disambiguationData":[TD([[makeQuery(id+"F5.imprint","IMPRINT",EDGE,{"disambiguationData":[TD([[subQ2,1.0]])],"derivedFrom":subQ1}),-1.0]])]});}
            var Q12;
            {var subQ0=sQuery(id+"F5.wireOp",EDGE,"E102.2.right");var subQ1=sQuery(id+"F5.wireOp",EDGE,"E98");var subQ2=makeQuery(id+"F5.imprint","INTERSECT",VERTEX,{"derivedFrom":[subQ1,subQ0]});Q12=makeQuery(id+"F5.imprint","IMPRINT",FACE,{"disambiguationData":[TD([[makeQuery(id+"F5.imprint","IMPRINT",EDGE,{"disambiguationData":[TD([[subQ2,1.0]])],"derivedFrom":subQ1}),1.0]])]});}
            var Q13;
            {var subQ4=sQuery(id+"F5.wireOp",EDGE,"E99");var subQ6=makeQuery(id+"F5.imprint","INTERSECT",VERTEX,{"derivedFrom":[sQuery(id+"F5.wireOp",EDGE,"E98"),subQ4]});Q13=makeQuery(id+"F5.imprint","IMPRINT",FACE,{"disambiguationData":[TD([[makeQuery(id+"F5.imprint","IMPRINT",EDGE,{"disambiguationData":[TD([[subQ6,1.0]])],"derivedFrom":subQ4}),1.0]])]});}
            var Q14;
            {var subQ5=sQuery(id+"F5.wireOp",EDGE,"E99");var subQ6=sQuery(id+"F5.wireOp",EDGE,"E98");var subQ7=makeQuery(id+"F5.imprint","INTERSECT",VERTEX,{"derivedFrom":[subQ6,subQ5]});Q14=makeQuery(id+"F5.imprint","IMPRINT",FACE,{"disambiguationData":[TD([[makeQuery(id+"F5.imprint","IMPRINT",EDGE,{"disambiguationData":[TD([[subQ7,1.0]])],"derivedFrom":subQ6}),1.0]])]});}
            var Q15;
            {var subQ0=sQuery(id+"F5.wireOp",EDGE,"E99");var subQ1=sQuery(id+"F5.wireOp",EDGE,"E98");var subQ2=makeQuery(id+"F5.imprint","INTERSECT",VERTEX,{"derivedFrom":[subQ1,subQ0]});Q15=makeQuery(id+"F5.imprint","IMPRINT",FACE,{"disambiguationData":[TD([[makeQuery(id+"F5.imprint","IMPRINT",EDGE,{"disambiguationData":[TD([[subQ2,1.0]])],"derivedFrom":subQ1}),-1.0]])]});}
            var Q16;
            {var subQ0=sQuery(id+"F5.wireOp",EDGE,"E102.2.endCap");Q16=makeQuery(id+"F5.imprint","IMPRINT",FACE,{"disambiguationData":[TD([[makeQuery(id+"F5.imprint","IMPRINT",EDGE,{"derivedFrom":subQ0}),-1.0]])]});}
            var Q17;
            {var subQ0=sQuery(id+"F5.wireOp",EDGE,"E102.2.startCap");Q17=makeQuery(id+"F5.imprint","IMPRINT",FACE,{"disambiguationData":[TD([[makeQuery(id+"F5.imprint","IMPRINT",EDGE,{"derivedFrom":subQ0}),-1.0]])]});}
            extrude(context, id + "F6", {"entities" : qUnion([Q0, Q1, Q2, Q3, Q4, Q5, Q6, Q7, Q8, Q9, Q10, Q11, Q12, Q13, Q14, Q15, Q16, Q17]), "operationType" : NewBodyOperationType.REMOVE, "oppositeDirection" : true, "depth" : 25 * mm});
        }
        {
            var Q0;
            Q0=makeQuery(id+"F1.opExtrude","CAP_FACE",FACE,{"disambiguationData":[OSD([sQuery(id+"F0.wireOp",EDGE,"E72.MirrorCS"),sQuery(id+"F0.wireOp",EDGE,"E73.MirrorCS"),sQuery(id+"F0.wireOp",EDGE,"E74.MirrorCS"),sQuery(id+"F0.wireOp",EDGE,"E75.MirrorCS"),sQuery(id+"F0.wireOp",EDGE,"E77.MirrorCS"),sQuery(id+"F0.wireOp",EDGE,"E78.MirrorCS"),sQuery(id+"F0.wireOp",EDGE,"E79.MirrorCS"),sQuery(id+"F0.wireOp",EDGE,"E80.MirrorCS")])],"isStart":false});
            var sketch = newSketch(context, id + "F7", { "sketchPlane" : qUnion([Q0])});
            skLineSegment(sketch, "E103", {"start": v(-44.5, -108.68) * mm, "end": v(99.69, -61.83) * mm});
            skLineSegment(sketch, "E104", {"start": v(113.1, -43.36) * mm, "end": v(77.12, -92.9) * mm});
            skLineSegment(sketch, "E105", {"start": v(-66.52, -101.53) * mm, "end": v(-0.65, -122.93) * mm});
            skPoint(sketch, "E106.end.orphan", {"position": v(65.22, -144.33) * mm});
            skArc(sketch, "E107.0.startCap", {"start": v(-43.92, -110.47) * mm, "mid": v(-46.29, -109.26) * mm, "end": v(-45.08, -106.9) * mm});
            skArc(sketch, "E107.0.endCap", {"start": v(99.1, -60.05) * mm, "mid": v(101.47, -61.25) * mm, "end": v(100.27, -63.62) * mm});
            skLineSegment(sketch, "E107.0.left", {"start": v(-45.08, -106.9) * mm, "end": v(99.1, -60.05) * mm});
            skLineSegment(sketch, "E107.0.right", {"start": v(-43.92, -110.47) * mm, "end": v(100.27, -63.62) * mm});
            skArc(sketch, "E107.1.startCap", {"start": v(-67.1, -103.31) * mm, "mid": v(-68.3, -100.95) * mm, "end": v(-65.94, -99.75) * mm});
            skArc(sketch, "E107.1.endCap", {"start": v(-0.07, -121.15) * mm, "mid": v(1.13, -123.5) * mm, "end": v(-1.23, -124.71) * mm});
            skLineSegment(sketch, "E107.1.left", {"start": v(-65.94, -99.75) * mm, "end": v(-0.07, -121.15) * mm});
            skLineSegment(sketch, "E107.1.right", {"start": v(-67.1, -103.31) * mm, "end": v(-1.23, -124.71) * mm});
            skArc(sketch, "E107.2.startCap", {"start": v(111.59, -42.26) * mm, "mid": v(114.2, -41.85) * mm, "end": v(114.62, -44.47) * mm});
            skArc(sketch, "E107.2.endCap", {"start": v(78.64, -94) * mm, "mid": v(76.02, -94.4) * mm, "end": v(75.6, -91.79) * mm});
            skLineSegment(sketch, "E107.2.left", {"start": v(114.62, -44.47) * mm, "end": v(78.64, -94) * mm});
            skLineSegment(sketch, "E107.2.right", {"start": v(111.59, -42.26) * mm, "end": v(75.6, -91.79) * mm});
            skSolve(sketch);
        }
        {
            var Q0;
            {var subQ4=sQuery(id+"F7.wireOp",EDGE,"E107.2.endCap");Q0=makeQuery(id+"F7.imprint","IMPRINT",FACE,{"disambiguationData":[TD([[makeQuery(id+"F7.imprint","IMPRINT",EDGE,{"derivedFrom":subQ4}),-1.0]])]});}
            var Q1;
            {var subQ5=sQuery(id+"F7.wireOp",EDGE,"E107.0.right");var subQ7=sQuery(id+"F7.wireOp",EDGE,"E104");var subQ8=makeQuery(id+"F7.imprint","INTERSECT",VERTEX,{"derivedFrom":[subQ7,subQ5]});Q1=makeQuery(id+"F7.imprint","IMPRINT",FACE,{"disambiguationData":[TD([[makeQuery(id+"F7.imprint","IMPRINT",EDGE,{"disambiguationData":[TD([[subQ8,-1.0]])],"derivedFrom":subQ7}),1.0]])]});}
            var Q2;
            {var subQ0=sQuery(id+"F7.wireOp",EDGE,"E107.0.right");var subQ1=sQuery(id+"F7.wireOp",EDGE,"E104");var subQ2=makeQuery(id+"F7.imprint","INTERSECT",VERTEX,{"derivedFrom":[subQ1,subQ0]});Q2=makeQuery(id+"F7.imprint","IMPRINT",FACE,{"disambiguationData":[TD([[makeQuery(id+"F7.imprint","IMPRINT",EDGE,{"disambiguationData":[TD([[subQ2,-1.0]])],"derivedFrom":subQ1}),-1.0]])]});}
            var Q3;
            {var subQ0=sQuery(id+"F7.wireOp",EDGE,"E104");var subQ1=sQuery(id+"F7.wireOp",EDGE,"E103");var subQ2=makeQuery(id+"F7.imprint","INTERSECT",VERTEX,{"derivedFrom":[subQ1,subQ0]});Q3=makeQuery(id+"F7.imprint","IMPRINT",FACE,{"disambiguationData":[TD([[makeQuery(id+"F7.imprint","IMPRINT",EDGE,{"disambiguationData":[TD([[subQ2,1.0]])],"derivedFrom":subQ1}),-1.0]])]});}
            var Q4;
            {var subQ0=sQuery(id+"F7.wireOp",EDGE,"E107.2.right");var subQ1=sQuery(id+"F7.wireOp",EDGE,"E103");var subQ2=makeQuery(id+"F7.imprint","INTERSECT",VERTEX,{"derivedFrom":[subQ1,subQ0]});Q4=makeQuery(id+"F7.imprint","IMPRINT",FACE,{"disambiguationData":[TD([[makeQuery(id+"F7.imprint","IMPRINT",EDGE,{"disambiguationData":[TD([[subQ2,1.0]])],"derivedFrom":subQ1}),1.0]])]});}
            var Q5;
            {var subQ5=sQuery(id+"F7.wireOp",EDGE,"E104");var subQ7=sQuery(id+"F7.wireOp",EDGE,"E103");var subQ8=makeQuery(id+"F7.imprint","INTERSECT",VERTEX,{"derivedFrom":[subQ7,subQ5]});Q5=makeQuery(id+"F7.imprint","IMPRINT",FACE,{"disambiguationData":[TD([[makeQuery(id+"F7.imprint","IMPRINT",EDGE,{"disambiguationData":[TD([[subQ8,1.0]])],"derivedFrom":subQ7}),1.0]])]});}
            var Q6;
            {var subQ5=sQuery(id+"F7.wireOp",EDGE,"E107.0.endCap");var subQ7=sQuery(id+"F7.wireOp",EDGE,"E104");var subQ8=makeQuery(id+"F7.imprint","INTERSECT",VERTEX,{"derivedFrom":[subQ7,subQ5]});Q6=makeQuery(id+"F7.imprint","IMPRINT",FACE,{"disambiguationData":[TD([[makeQuery(id+"F7.imprint","IMPRINT",EDGE,{"disambiguationData":[TD([[subQ8,1.0]])],"derivedFrom":subQ7}),-1.0]])]});}
            var Q7;
            {var subQ0=sQuery(id+"F7.wireOp",EDGE,"E107.0.endCap");var subQ1=sQuery(id+"F7.wireOp",EDGE,"E104");var subQ2=makeQuery(id+"F7.imprint","INTERSECT",VERTEX,{"derivedFrom":[subQ1,subQ0]});Q7=makeQuery(id+"F7.imprint","IMPRINT",FACE,{"disambiguationData":[TD([[makeQuery(id+"F7.imprint","IMPRINT",EDGE,{"disambiguationData":[TD([[subQ2,1.0]])],"derivedFrom":subQ1}),1.0]])]});}
            var Q8;
            {var subQ4=sQuery(id+"F7.wireOp",EDGE,"E107.2.startCap");Q8=makeQuery(id+"F7.imprint","IMPRINT",FACE,{"disambiguationData":[TD([[makeQuery(id+"F7.imprint","IMPRINT",EDGE,{"derivedFrom":subQ4}),-1.0]])]});}
            var Q9;
            {var subQ4=sQuery(id+"F7.wireOp",EDGE,"E104");var subQ6=makeQuery(id+"F7.imprint","INTERSECT",VERTEX,{"derivedFrom":[sQuery(id+"F7.wireOp",EDGE,"E103"),subQ4]});Q9=makeQuery(id+"F7.imprint","IMPRINT",FACE,{"disambiguationData":[TD([[makeQuery(id+"F7.imprint","IMPRINT",EDGE,{"disambiguationData":[TD([[subQ6,1.0]])],"derivedFrom":subQ4}),1.0]])]});}
            var Q10;
            {var subQ0=sQuery(id+"F7.wireOp",EDGE,"E107.2.right");var subQ1=sQuery(id+"F7.wireOp",EDGE,"E103");var subQ2=makeQuery(id+"F7.imprint","INTERSECT",VERTEX,{"derivedFrom":[subQ1,subQ0]});Q10=makeQuery(id+"F7.imprint","IMPRINT",FACE,{"disambiguationData":[TD([[makeQuery(id+"F7.imprint","IMPRINT",EDGE,{"disambiguationData":[TD([[subQ2,1.0]])],"derivedFrom":subQ1}),-1.0]])]});}
            extrude(context, id + "F8", {"entities" : qUnion([Q0, Q1, Q2, Q3, Q4, Q5, Q6, Q7, Q8, Q9, Q10]), "operationType" : NewBodyOperationType.REMOVE, "oppositeDirection" : true, "depth" : 25 * mm});
        }
        {
            var Q0;
            Q0=makeQuery(id+"F1.opExtrude","CAP_EDGE",EDGE,{"disambiguationData":[OSD([sQuery(id+"F0.wireOp",EDGE,"E83.MirrorCS")])],"isStart":true});
            var Q1;
            Q1=makeQuery(id+"F1.opExtrude","CAP_EDGE",EDGE,{"disambiguationData":[OSD([sQuery(id+"F0.wireOp",EDGE,"E83.MirrorCS")])],"isStart":false});
            var Q2;
            Q2=makeQuery(id+"F1.opExtrude","CAP_EDGE",EDGE,{"disambiguationData":[OSD([sQuery(id+"F0.wireOp",EDGE,"E82")])],"isStart":false});
            var Q3;
            Q3=makeQuery(id+"F1.opExtrude","CAP_EDGE",EDGE,{"disambiguationData":[OSD([sQuery(id+"F0.wireOp",EDGE,"E82")])],"isStart":true});
            fillet(context, id + "F9", {"entities" : qUnion([Q0, Q1, Q2, Q3]), "radius" : 5 * mm, "tangentPropagation" : true, "allowEdgeOverflow" : false});
        }
        {
            var Q0;
            Q0=makeQuery(id+"F1.opExtrude","SWEPT_FACE",FACE,{"disambiguationData":[OSD([sQuery(id+"F0.wireOp",EDGE,"E81")])]});
            var sketch = newSketch(context, id + "F10", { "sketchPlane" : qUnion([Q0])});
            skLineSegment(sketch, "E108", {"start": v(-28.32, 17.5) * mm, "end": v(28.32, 17.5) * mm, "construction": true});
            skLineSegment(sketch, "E109", {"start": v(0, 35) * mm, "end": v(0, 0) * mm, "construction": true});
            skCircle(sketch, "E110.cCircle", {"center": v(0, 17.5) * mm, "radius": 5.6 * mm, "construction": true});
            skLineSegment(sketch, "E110.0", {"start": v(-3.23, 23.1) * mm, "end": v(3.23, 23.1) * mm});
            skLineSegment(sketch, "E110.1", {"start": v(3.23, 23.1) * mm, "end": v(6.47, 17.5) * mm});
            skLineSegment(sketch, "E110.2", {"start": v(6.47, 17.5) * mm, "end": v(3.23, 11.9) * mm});
            skLineSegment(sketch, "E110.3", {"start": v(3.23, 11.9) * mm, "end": v(-3.23, 11.9) * mm});
            skLineSegment(sketch, "E110.4", {"start": v(-3.23, 11.9) * mm, "end": v(-6.47, 17.5) * mm});
            skLineSegment(sketch, "E110.5", {"start": v(-6.47, 17.5) * mm, "end": v(-3.23, 23.1) * mm});
            skPoint(sketch, "E110.0.midPoint", {"position": v(0, 23.1) * mm});
            skSolve(sketch);
        }
        {
            var Q0;
            Q0=makeQuery(id+"F10.imprint","IMPRINT",FACE,{"disambiguationData":[TD([[makeQuery(id+"F10.imprint","IMPRINT",EDGE,{"derivedFrom":sQuery(id+"F10.wireOp",EDGE,"E110.0")}),1.0]])]});
            var sketch = newSketch(context, id + "F11", { "sketchPlane" : qUnion([Q0])});
            skCircle(sketch, "E111", {"center": v(0, 17.5) * mm, "radius": 3.25 * mm});
            skSolve(sketch);
        }
        {
            var Q0;
            Q0=qSketchRegion(id+"F10",true);
            extrude(context, id + "F12", {"entities" : qUnion([Q0]), "operationType" : NewBodyOperationType.REMOVE, "oppositeDirection" : true, "depth" : 5 * mm});
        }
        {
            var Q0;
            Q0=makeQuery(id+"F11.imprint","IMPRINT",FACE,{"disambiguationData":[TD([[makeQuery(id+"F11.imprint","IMPRINT",EDGE,{"derivedFrom":sQuery(id+"F11.wireOp",EDGE,"E111")}),1.0]])]});
            var Q1;
            Q1=sQuery(id+"F11.wireOp",EDGE,"E111");
            extrude(context, id + "F13", {"entities" : qUnion([Q0]), "operationType" : NewBodyOperationType.REMOVE, "surfaceEntities" : qUnion([Q1]), "oppositeDirection" : true, "depth" : 15 * mm});
        }
        {
            var Q0;
            Q0=makeQuery(id+"F1.opExtrude","SWEPT_FACE",FACE,{"disambiguationData":[OSD([sQuery(id+"F0.wireOp",EDGE,"E60")])]});
            var sketch = newSketch(context, id + "F14", { "sketchPlane" : qUnion([Q0])});
            skLineSegment(sketch, "E112.bottom", {"start": v(-22.07, 35) * mm, "end": v(17.93, 35) * mm});
            skLineSegment(sketch, "E112.top", {"start": v(-22.07, 10) * mm, "end": v(17.93, 10) * mm});
            skLineSegment(sketch, "E112.left", {"start": v(-22.07, 35) * mm, "end": v(-22.07, 10) * mm});
            skLineSegment(sketch, "E112.right", {"start": v(17.93, 35) * mm, "end": v(17.93, 10) * mm});
            skSolve(sketch);
        }
        {
            var Q0;
            Q0=makeQuery(id+"F14.imprint","IMPRINT",FACE,{"disambiguationData":[TD([[makeQuery(id+"F14.imprint","IMPRINT",EDGE,{"derivedFrom":sQuery(id+"F14.wireOp",EDGE,"E112.bottom")}),1.0]])]});
            extrude(context, id + "F15", {"entities" : qUnion([Q0]), "operationType" : NewBodyOperationType.REMOVE, "oppositeDirection" : true, "depth" : 4.5 * mm});
        }
        {
            var Q0;
            Q0=makeQuery(id+"F1.opExtrude","SWEPT_FACE",FACE,{"disambiguationData":[OSD([sQuery(id+"F0.wireOp",EDGE,"E78.MirrorCS")])]});
            var sketch = newSketch(context, id + "F16", { "sketchPlane" : qUnion([Q0])});
            skLineSegment(sketch, "E113.bottom", {"start": v(-17.93, 35) * mm, "end": v(22.07, 35) * mm});
            skLineSegment(sketch, "E113.top", {"start": v(-17.93, 10) * mm, "end": v(22.07, 10) * mm});
            skLineSegment(sketch, "E113.left", {"start": v(-17.93, 35) * mm, "end": v(-17.93, 10) * mm});
            skLineSegment(sketch, "E113.right", {"start": v(22.07, 35) * mm, "end": v(22.07, 10) * mm});
            skSolve(sketch);
        }
        {
            var Q0;
            Q0 = qSketchRegion(id + "F16", true);
            extrude(context, id + "F17", {"entities" : qUnion([Q0]), "operationType" : NewBodyOperationType.REMOVE, "oppositeDirection" : true, "depth" : 4.5 * mm});
        }
        {
            var Q0;
            Q0=makeQuery(id+"F1.opExtrude","SWEPT_FACE",FACE,{"disambiguationData":[OSD([sQuery(id+"F0.wireOp",EDGE,"E81")])]});
            extrude(context, id + "F18", {"entities" : qUnion([Q0]), "depth" : 6.6 * mm, "offsetDistance" : 25 * mm});
        }
        {
            var Q0;
            Q0=makeQuery(id+"F18.opExtrude","CAP_FACE",FACE,{"disambiguationData":[OSD([sQuery(id+"F0.wireOp",EDGE,"E81")])],"isStart":false});
            var sketch = newSketch(context, id + "F19", { "sketchPlane" : qUnion([Q0])});
            skLineSegment(sketch, "E114.bottom", {"start": v(12.72, 26.83) * mm, "end": v(-12.73, 26.83) * mm});
            skLineSegment(sketch, "E114.top", {"start": v(12.72, 8.38) * mm, "end": v(-12.73, 8.38) * mm});
            skLineSegment(sketch, "E114.left", {"start": v(13.72, 25.83) * mm, "end": v(13.72, 9.38) * mm});
            skLineSegment(sketch, "E114.right", {"start": v(-13.73, 25.83) * mm, "end": v(-13.73, 9.38) * mm});
            skPoint(sketch, "E114.middle", {"position": v(0, 17.6) * mm});
            skPoint(sketch, "E114.middle.positionSnap0", {"position": v(0, 11.9) * mm});
            skPoint(sketch, "E114.centerSnap0", {"position": v(0, 11.9) * mm});
            skPoint(sketch, "E115.visualSharp", {"position": v(-13.73, 26.83) * mm});
            skArc(sketch, "E115.filletArc", {"start": v(-12.73, 26.83) * mm, "mid": v(-13.43, 26.54) * mm, "end": v(-13.73, 25.83) * mm});
            skPoint(sketch, "E116.visualSharp", {"position": v(13.72, 26.83) * mm});
            skArc(sketch, "E116.filletArc", {"start": v(13.72, 25.83) * mm, "mid": v(13.43, 26.54) * mm, "end": v(12.72, 26.83) * mm});
            skPoint(sketch, "E117.visualSharp", {"position": v(13.72, 8.38) * mm});
            skArc(sketch, "E117.filletArc", {"start": v(12.72, 8.38) * mm, "mid": v(13.43, 8.68) * mm, "end": v(13.72, 9.38) * mm});
            skPoint(sketch, "E118.visualSharp", {"position": v(-13.73, 8.38) * mm});
            skArc(sketch, "E118.filletArc", {"start": v(-13.73, 9.38) * mm, "mid": v(-13.43, 8.68) * mm, "end": v(-12.73, 8.38) * mm});
            skSolve(sketch);
        }
        {
            var Q0;
            Q0 = qSketchRegion(id + "F19", true);
            extrude(context, id + "F20", {"entities" : qUnion([Q0]), "operationType" : NewBodyOperationType.REMOVE, "oppositeDirection" : true, "depth" : 25 * mm, "offsetDistance" : 25 * mm});
        }
    });
